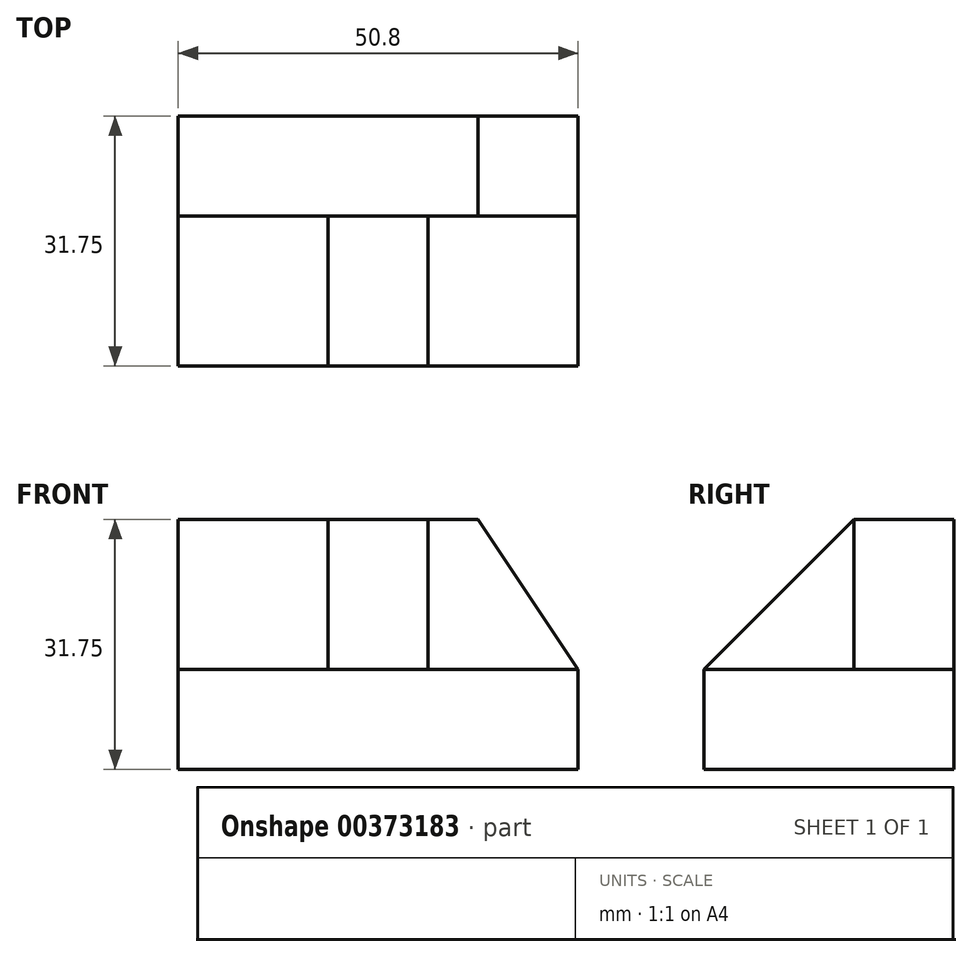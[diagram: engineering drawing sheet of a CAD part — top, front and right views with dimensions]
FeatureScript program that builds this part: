
annotation { "Feature Type Name" : "Feature", "Feature Type Description" : "" }
export const myFeature = defineFeature(function(context is Context, id is Id, definition is map)
    precondition{}
    {
        {
            var Q0;
            Q0=qCreatedBy(makeId("Front.planeOp"),FACE);
            var sketch = newSketch(context, id + "F0", { "sketchPlane" : qUnion([Q0])});
            skLineSegment(sketch, "E0", {"start": v(-18.53, 31.75) * mm, "end": v(-18.53, 0) * mm});
            skLineSegment(sketch, "E1", {"start": v(-18.53, 0) * mm, "end": v(32.27, 0) * mm});
            skLineSegment(sketch, "E2", {"start": v(-18.53, 31.75) * mm, "end": v(32.27, 31.75) * mm});
            skLineSegment(sketch, "E3", {"start": v(32.27, 31.75) * mm, "end": v(32.27, 0) * mm});
            skSolve(sketch);
        }
        {
            var Q0;
            Q0=makeQuery(id+"F0.imprint","IMPRINT",FACE,{"disambiguationData":[TD([[makeQuery(id+"F0.imprint","IMPRINT",EDGE,{"derivedFrom":sQuery(id+"F0.wireOp",EDGE,"E0")}),1.0]])]});
            extrude(context, id + "F1", {"entities" : qUnion([Q0]), "depth" : 31.75 * mm});
        }
        {
            var Q0;
            Q0=makeQuery(id+"F1.opExtrude","SWEPT_FACE",FACE,{"disambiguationData":[OSD([sQuery(id+"F0.wireOp",EDGE,"E3")])]});
            var sketch = newSketch(context, id + "F2", { "sketchPlane" : qUnion([Q0])});
            skLineSegment(sketch, "E4", {"start": v(-31.75, 12.7) * mm, "end": v(-12.7, 31.75) * mm});
            skSolve(sketch);
        }
        {
            var Q0;
            {var subQ0=sQuery(id+"F2.wireOp",EDGE,"E4");Q0=makeQuery(id+"F2.imprint","IMPRINT",FACE,{"disambiguationData":[TD([[makeQuery(id+"F2.imprint","IMPRINT",EDGE,{"derivedFrom":subQ0}),1.0]])]});}
            extrude(context, id + "F3", {"entities" : qUnion([Q0]), "operationType" : NewBodyOperationType.REMOVE, "oppositeDirection" : true, "depth" : 50.8 * mm});
        }
        {
            var Q0;
            Q0=makeQuery(id+"F1.opExtrude","SWEPT_FACE",FACE,{"disambiguationData":[OSD([sQuery(id+"F0.wireOp",EDGE,"E0")])]});
            var sketch = newSketch(context, id + "F4", { "sketchPlane" : qUnion([Q0])});
            skLineSegment(sketch, "E5", {"start": v(12.7, 31.75) * mm, "end": v(12.7, 12.7) * mm});
            skLineSegment(sketch, "E6", {"start": v(12.7, 12.7) * mm, "end": v(31.75, 12.7) * mm});
            skSolve(sketch);
        }
        {
            var Q0;
            Q0=makeQuery(id+"F4.imprint","IMPRINT",FACE,{"disambiguationData":[TD([[makeQuery(id+"F4.imprint","IMPRINT",EDGE,{"derivedFrom":sQuery(id+"F4.wireOp",EDGE,"E5")}),1.0]])]});
            extrude(context, id + "F5", {"entities" : qUnion([Q0]), "operationType" : NewBodyOperationType.REMOVE, "oppositeDirection" : true, "depth" : 19.05 * mm});
        }
        {
            var Q0;
            Q0=makeQuery(id+"F1.opExtrude","SWEPT_FACE",FACE,{"disambiguationData":[OSD([sQuery(id+"F0.wireOp",EDGE,"E3")])]});
            var sketch = newSketch(context, id + "F6", { "sketchPlane" : qUnion([Q0])});
            skLineSegment(sketch, "E7", {"start": v(-31.75, 12.7) * mm, "end": v(-12.7, 12.7) * mm});
            skLineSegment(sketch, "E8", {"start": v(-12.7, 12.7) * mm, "end": v(-12.7, 31.75) * mm});
            skSolve(sketch);
        }
        {
            var Q0;
            Q0=makeQuery(id+"F6.imprint","IMPRINT",FACE,{"disambiguationData":[TD([[makeQuery(id+"F6.imprint","IMPRINT",EDGE,{"derivedFrom":sQuery(id+"F6.wireOp",EDGE,"E7")}),1.0]])]});
            extrude(context, id + "F7", {"entities" : qUnion([Q0]), "operationType" : NewBodyOperationType.REMOVE, "oppositeDirection" : true, "depth" : 19.05 * mm});
        }
        {
            var Q0;
            Q0=makeQuery(id+"F7.boolean.opBoolean","COPY",FACE,{"derivedFrom":makeQuery(id+"F7.opExtrude","SWEPT_FACE",FACE,{"disambiguationData":[OSD([sQuery(id+"F6.wireOp",EDGE,"E8")])]})});
            var sketch = newSketch(context, id + "F8", { "sketchPlane" : qUnion([Q0])});
            skLineSegment(sketch, "E9", {"start": v(32.27, 12.7) * mm, "end": v(19.57, 31.75) * mm});
            skSolve(sketch);
        }
        {
            var Q0;
            {var subQ0=sQuery(id+"F8.wireOp",EDGE,"E9");Q0=makeQuery(id+"F8.imprint","IMPRINT",FACE,{"disambiguationData":[TD([[makeQuery(id+"F8.imprint","IMPRINT",EDGE,{"derivedFrom":subQ0}),-1.0]])]});}
            extrude(context, id + "F9", {"entities" : qUnion([Q0]), "operationType" : NewBodyOperationType.REMOVE, "oppositeDirection" : true, "depth" : 12.7 * mm});
        }
    });
